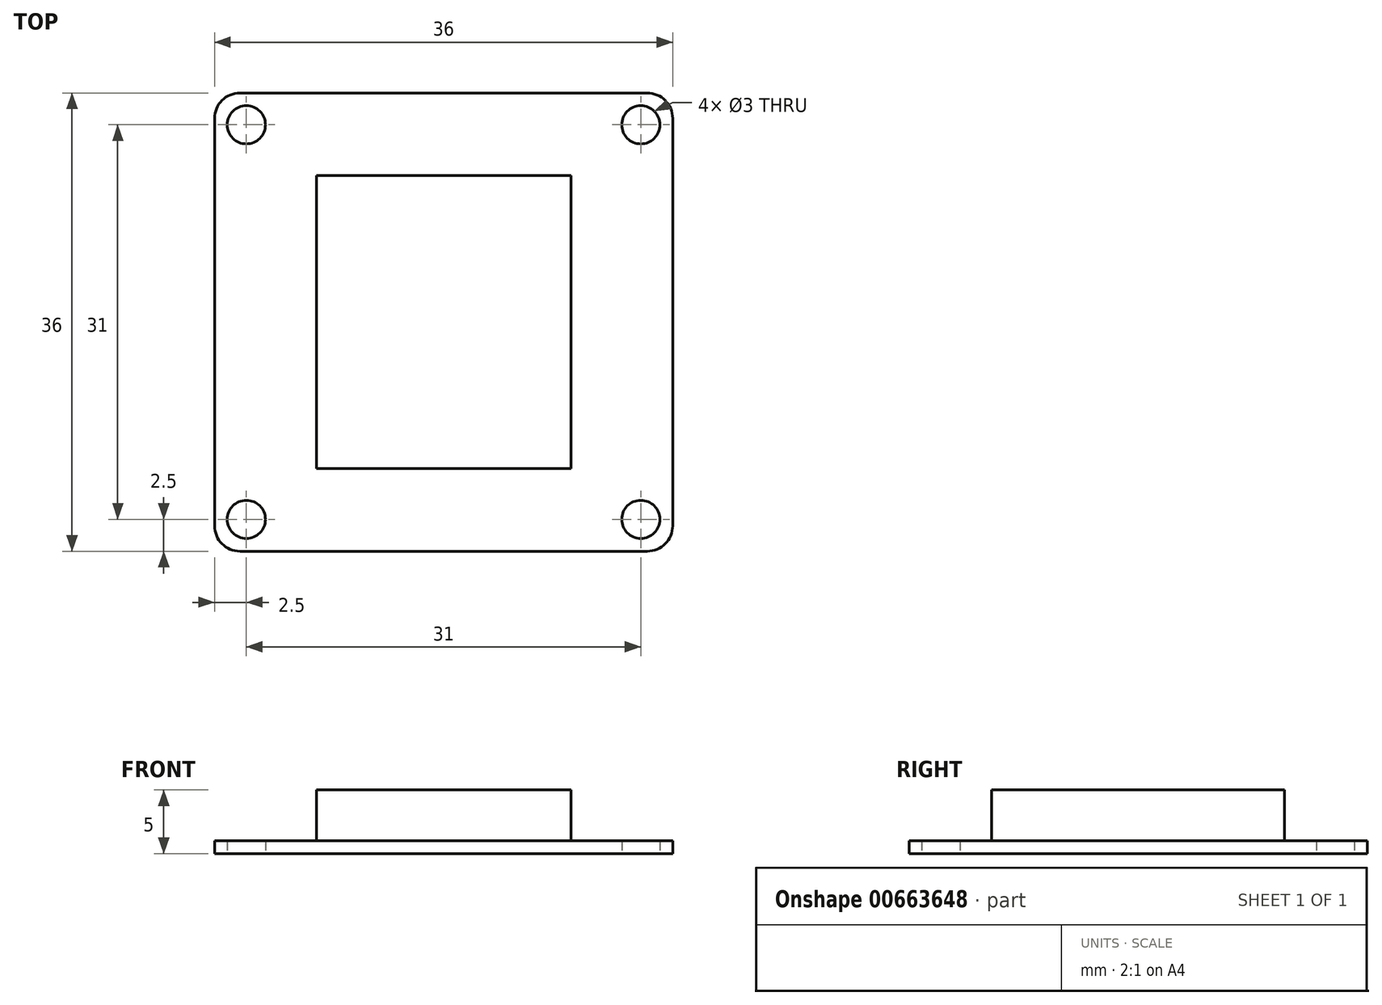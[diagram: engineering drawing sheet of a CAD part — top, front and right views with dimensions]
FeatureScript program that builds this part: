
annotation { "Feature Type Name" : "Feature", "Feature Type Description" : "" }
export const myFeature = defineFeature(function(context is Context, id is Id, definition is map)
    precondition{}
    {
        {
            var Q0;
            Q0=qCreatedBy(makeId("Top.planeOp"),FACE);
            var sketch = newSketch(context, id + "F0", { "sketchPlane" : qUnion([Q0])});
            skLineSegment(sketch, "E0.bottom", {"start": v(-16, 18) * mm, "end": v(16, 18) * mm});
            skLineSegment(sketch, "E0.top", {"start": v(-16, -18) * mm, "end": v(16, -18) * mm});
            skLineSegment(sketch, "E0.left", {"start": v(-18, 16) * mm, "end": v(-18, -16) * mm});
            skLineSegment(sketch, "E0.right", {"start": v(18, 16) * mm, "end": v(18, -16) * mm});
            skPoint(sketch, "E0.middle", {"position": v(0, 0) * mm});
            skPoint(sketch, "E1.visualSharp", {"position": v(-18, 18) * mm});
            skArc(sketch, "E1.filletArc", {"start": v(-16, 18) * mm, "mid": v(-17.41, 17.41) * mm, "end": v(-18, 16) * mm});
            skPoint(sketch, "E2.visualSharp", {"position": v(18, 18) * mm});
            skArc(sketch, "E2.filletArc", {"start": v(18, 16) * mm, "mid": v(17.41, 17.41) * mm, "end": v(16, 18) * mm});
            skPoint(sketch, "E3.visualSharp", {"position": v(18, -18) * mm});
            skArc(sketch, "E3.filletArc", {"start": v(16, -18) * mm, "mid": v(17.41, -17.41) * mm, "end": v(18, -16) * mm});
            skPoint(sketch, "E4.visualSharp", {"position": v(-18, -18) * mm});
            skArc(sketch, "E4.filletArc", {"start": v(-18, -16) * mm, "mid": v(-17.41, -17.41) * mm, "end": v(-16, -18) * mm});
            skLineSegment(sketch, "E5", {"start": v(0, 0) * mm, "end": v(0, -18) * mm, "construction": true});
            skLineSegment(sketch, "E6", {"start": v(-18, 0) * mm, "end": v(0, 0) * mm, "construction": true});
            skCircle(sketch, "E7", {"center": v(-15.5, -15.5) * mm, "radius": 1.5 * mm});
            skCircle(sketch, "E8.MirrorC", {"center": v(15.5, -15.5) * mm, "radius": 1.5 * mm});
            skCircle(sketch, "E9.MirrorC", {"center": v(-15.5, 15.5) * mm, "radius": 1.5 * mm});
            skCircle(sketch, "E10.MirrorC", {"center": v(15.5, 15.5) * mm, "radius": 1.5 * mm});
            skSolve(sketch);
        }
        {
            var Q0;
            Q0 = qSketchRegion(id + "F0", true);
            extrude(context, id + "F1", {"entities" : qUnion([Q0]), "depth" : 1 * mm, "offsetDistance" : 25 * mm});
        }
        {
            var Q0;
            Q0=makeQuery(id+"F1.opExtrude","CAP_FACE",FACE,{"disambiguationData":[OSD([sQuery(id+"F0.wireOp",EDGE,"E0.bottom"),sQuery(id+"F0.wireOp",EDGE,"E0.top"),sQuery(id+"F0.wireOp",EDGE,"E0.left"),sQuery(id+"F0.wireOp",EDGE,"E0.right"),sQuery(id+"F0.wireOp",EDGE,"E1.filletArc"),sQuery(id+"F0.wireOp",EDGE,"E2.filletArc"),sQuery(id+"F0.wireOp",EDGE,"E3.filletArc"),sQuery(id+"F0.wireOp",EDGE,"E4.filletArc"),sQuery(id+"F0.wireOp",EDGE,"E7"),sQuery(id+"F0.wireOp",EDGE,"E8.MirrorC"),sQuery(id+"F0.wireOp",EDGE,"E9.MirrorC"),sQuery(id+"F0.wireOp",EDGE,"E10.MirrorC")])],"isStart":false});
            var sketch = newSketch(context, id + "F2", { "sketchPlane" : qUnion([Q0])});
            skLineSegment(sketch, "E11.bottom", {"start": v(-10, 11.5) * mm, "end": v(10, 11.5) * mm});
            skLineSegment(sketch, "E11.top", {"start": v(-10, -11.5) * mm, "end": v(10, -11.5) * mm});
            skLineSegment(sketch, "E11.left", {"start": v(-10, 11.5) * mm, "end": v(-10, -11.5) * mm});
            skLineSegment(sketch, "E11.right", {"start": v(10, 11.5) * mm, "end": v(10, -11.5) * mm});
            skPoint(sketch, "E11.middle", {"position": v(0, 0) * mm});
            skSolve(sketch);
        }
        {
            var Q0;
            Q0 = qSketchRegion(id + "F2", true);
            extrude(context, id + "F3", {"entities" : qUnion([Q0]), "operationType" : NewBodyOperationType.ADD, "depth" : 4 * mm, "offsetDistance" : 25 * mm});
        }
    });
